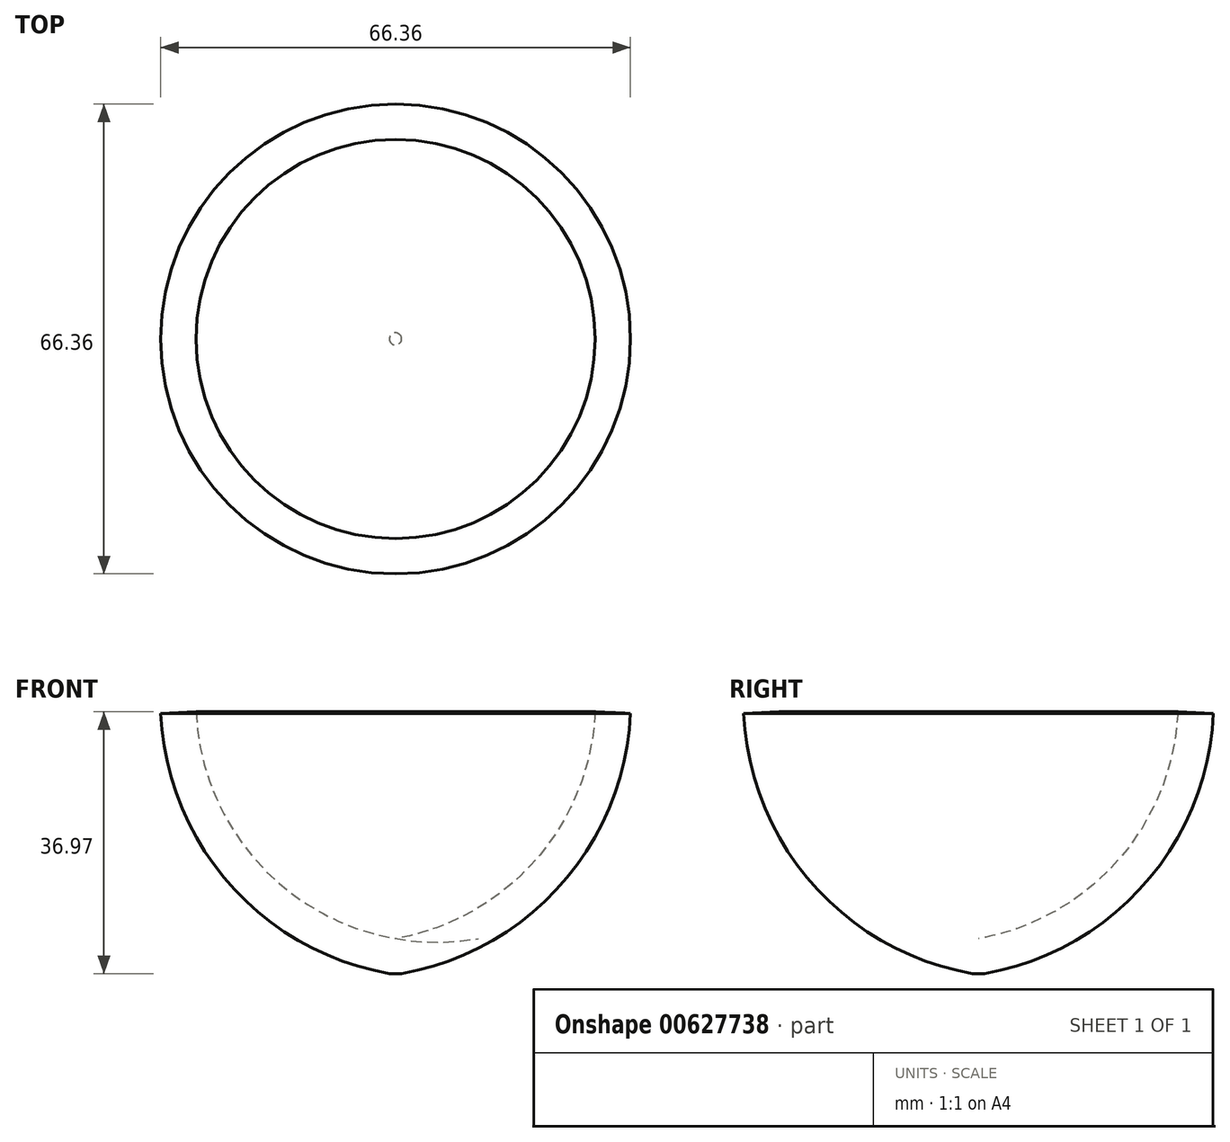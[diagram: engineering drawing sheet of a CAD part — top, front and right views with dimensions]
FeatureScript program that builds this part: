
annotation { "Feature Type Name" : "Feature", "Feature Type Description" : "" }
export const myFeature = defineFeature(function(context is Context, id is Id, definition is map)
    precondition{}
    {
        {
            var Q0;
            Q0=qCreatedBy(makeId("Front.planeOp"),FACE);
            var sketch = newSketch(context, id + "F0", { "sketchPlane" : qUnion([Q0])});
            skArc(sketch, "E0", {"start": v(-28.19, 32.04) * mm, "mid": v(-19.73, 11.06) * mm, "end": v(0, 0) * mm});
            skArc(sketch, "E1.0", {"start": v(-33.18, 31.81) * mm, "mid": v(-23.48, 7.76) * mm, "end": v(-0.86, -4.93) * mm});
            skLineSegment(sketch, "E2", {"start": v(-33.18, 31.81) * mm, "end": v(-28.19, 32.04) * mm});
            skLineSegment(sketch, "E3", {"start": v(0, 0) * mm, "end": v(0, -4.93) * mm});
            skLineSegment(sketch, "E4", {"start": v(-0.86, -4.93) * mm, "end": v(0, -4.93) * mm});
            skSolve(sketch);
        }
        {
            var Q0;
            Q0=makeQuery(id+"F0.imprint","IMPRINT",FACE,{"disambiguationData":[TD([[makeQuery(id+"F0.imprint","IMPRINT",EDGE,{"derivedFrom":sQuery(id+"F0.wireOp",EDGE,"E0")}),-1.0]])]});
            var Q1;
            Q1=sQuery(id+"F0.wireOp",EDGE,"E3");
            revolve(context, id + "F1", {"entities" : qUnion([Q0]), "axis" : qUnion([Q1]), "revolveType" : RevolveType.FULL});
        }
    });
